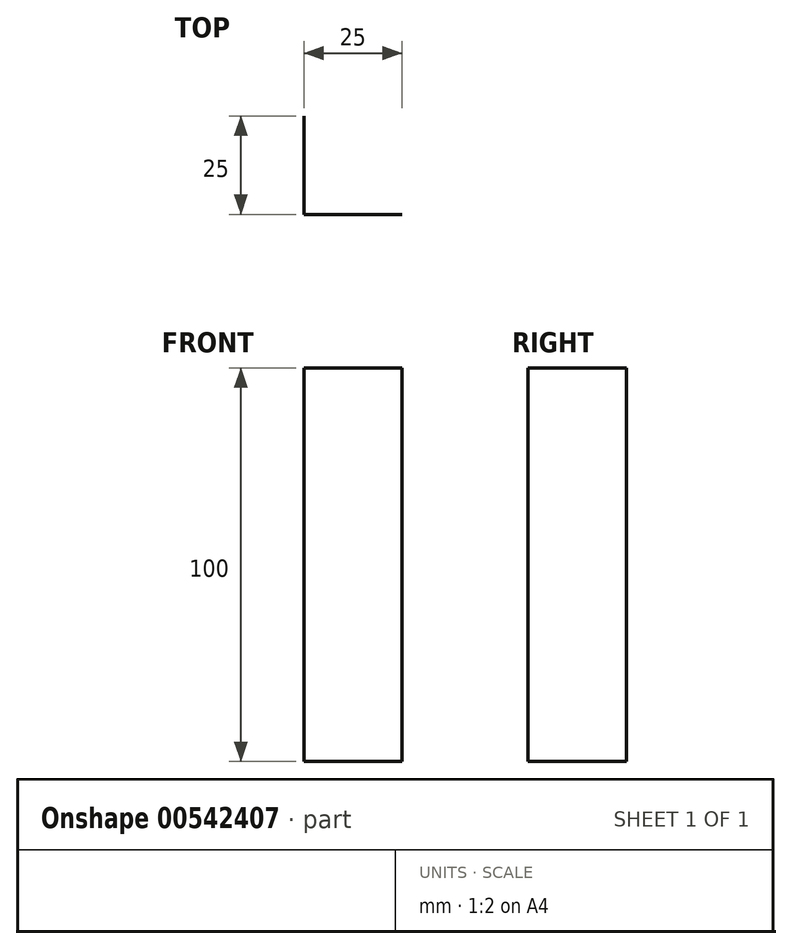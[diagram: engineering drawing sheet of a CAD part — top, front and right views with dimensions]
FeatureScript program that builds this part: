
annotation { "Feature Type Name" : "Feature", "Feature Type Description" : "" }
export const myFeature = defineFeature(function(context is Context, id is Id, definition is map)
    precondition{}
    {
        {
            var Q0;
            Q0=qCreatedBy(makeId("Top.planeOp"),FACE);
            var sketch = newSketch(context, id + "F0", { "sketchPlane" : qUnion([Q0])});
            skLineSegment(sketch, "E0", {"start": v(0, 25) * mm, "end": v(0, 0) * mm});
            skLineSegment(sketch, "E1", {"start": v(0, 0) * mm, "end": v(25, 0) * mm});
            skSolve(sketch);
        }
        {
            var Q0;
            Q0=sQuery(id+"F0.wireOp",EDGE,"E1");
            var Q1;
            Q1=sQuery(id+"F0.wireOp",EDGE,"E0");
            extrude(context, id + "F1", {"bodyType" : ToolBodyType.SURFACE, "surfaceEntities" : qUnion([Q0, Q1]), "depth" : 100 * mm, "offsetDistance" : 25 * mm});
        }
    });
